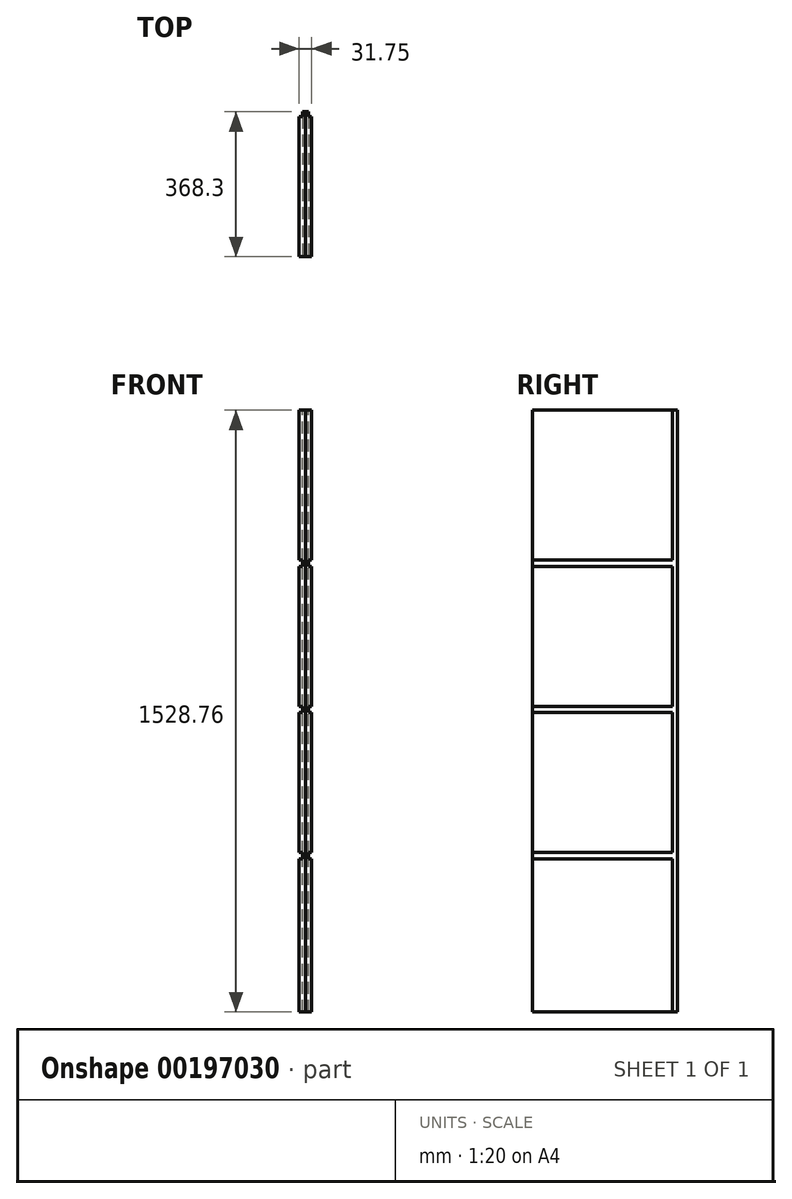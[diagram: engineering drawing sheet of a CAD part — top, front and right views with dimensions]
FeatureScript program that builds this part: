
annotation { "Feature Type Name" : "Feature", "Feature Type Description" : "" }
export const myFeature = defineFeature(function(context is Context, id is Id, definition is map)
    precondition{}
    {
        {
            var Q0;
            Q0=qCreatedBy(makeId("Top.planeOp"),FACE);
            var sketch = newSketch(context, id + "F0", { "sketchPlane" : qUnion([Q0])});
            skLineSegment(sketch, "E0.bottom", {"start": v(0, 0) * mm, "end": v(-15.88, 0) * mm});
            skLineSegment(sketch, "E0.top", {"start": v(0, 368.3) * mm, "end": v(-15.88, 368.3) * mm});
            skLineSegment(sketch, "E0.left", {"start": v(0, 0) * mm, "end": v(0, 368.3) * mm});
            skLineSegment(sketch, "E0.right", {"start": v(-15.88, 0) * mm, "end": v(-15.88, 368.3) * mm});
            skSolve(sketch);
        }
        {
            var Q0;
            Q0=makeQuery(id+"F0.imprint","IMPRINT",FACE,{"disambiguationData":[TD([[makeQuery(id+"F0.imprint","IMPRINT",EDGE,{"derivedFrom":sQuery(id+"F0.wireOp",EDGE,"E0.bottom")}),-1.0]])]});
            extrude(context, id + "F1", {"entities" : qUnion([Q0]), "depth" : 1528.76 * mm});
        }
        {
            var Q0;
            Q0=makeQuery(id+"F1.opExtrude","SWEPT_FACE",FACE,{"disambiguationData":[OSD([sQuery(id+"F0.wireOp",EDGE,"E0.bottom")])]});
            var sketch = newSketch(context, id + "F2", { "sketchPlane" : qUnion([Q0])});
            skLineSegment(sketch, "E1.bottom", {"start": v(0, 404.81) * mm, "end": v(-7.94, 404.81) * mm});
            skLineSegment(sketch, "E1.top", {"start": v(0, 388.94) * mm, "end": v(-7.94, 388.94) * mm});
            skLineSegment(sketch, "E1.left", {"start": v(0, 404.81) * mm, "end": v(0, 388.94) * mm});
            skLineSegment(sketch, "E1.right", {"start": v(-7.94, 404.81) * mm, "end": v(-7.94, 388.94) * mm});
            skLineSegment(sketch, "E2.bottom", {"start": v(0, 776.29) * mm, "end": v(-7.94, 776.29) * mm});
            skLineSegment(sketch, "E2.top", {"start": v(0, 760.41) * mm, "end": v(-7.94, 760.41) * mm});
            skLineSegment(sketch, "E2.left", {"start": v(0, 776.29) * mm, "end": v(0, 760.41) * mm});
            skLineSegment(sketch, "E2.right", {"start": v(-7.94, 776.29) * mm, "end": v(-7.94, 760.41) * mm});
            skLineSegment(sketch, "E3.bottom", {"start": v(0, 1147.76) * mm, "end": v(-7.94, 1147.76) * mm});
            skLineSegment(sketch, "E3.top", {"start": v(0, 1131.89) * mm, "end": v(-7.94, 1131.89) * mm});
            skLineSegment(sketch, "E3.left", {"start": v(0, 1147.76) * mm, "end": v(0, 1131.89) * mm});
            skLineSegment(sketch, "E3.right", {"start": v(-7.94, 1147.76) * mm, "end": v(-7.94, 1131.89) * mm});
            skLineSegment(sketch, "E4.bottom", {"start": v(0, 1516.06) * mm, "end": v(-7.94, 1516.06) * mm});
            skLineSegment(sketch, "E4.top", {"start": v(0, 1531.94) * mm, "end": v(-7.94, 1531.94) * mm});
            skLineSegment(sketch, "E4.left", {"start": v(0, 1516.06) * mm, "end": v(0, 1531.94) * mm});
            skLineSegment(sketch, "E4.right", {"start": v(-7.94, 1516.06) * mm, "end": v(-7.94, 1531.94) * mm});
            skLineSegment(sketch, "E5", {"start": v(-15.88, 0) * mm, "end": v(-15.88, -7.94) * mm, "construction": true});
            skLineSegment(sketch, "E6", {"start": v(-15.88, -7.94) * mm, "end": v(0, -7.94) * mm, "construction": true});
            skLineSegment(sketch, "E7", {"start": v(0, -7.94) * mm, "end": v(0, 0) * mm, "construction": true});
            skLineSegment(sketch, "E8", {"start": v(0, 0) * mm, "end": v(-15.88, 0) * mm, "construction": true});
            skLineSegment(sketch, "E9.bottom", {"start": v(0, -7.94) * mm, "end": v(1508.13, -7.94) * mm, "construction": true});
            skLineSegment(sketch, "E9.top", {"start": v(0, 7.94) * mm, "end": v(1508.13, 7.94) * mm, "construction": true});
            skLineSegment(sketch, "E9.left", {"start": v(0, -7.94) * mm, "end": v(0, 7.94) * mm, "construction": true});
            skLineSegment(sketch, "E9.right", {"start": v(1508.13, -7.94) * mm, "end": v(1508.13, 7.94) * mm, "construction": true});
            skSolve(sketch);
        }
        {
            var Q0;
            Q0=makeQuery(id+"F2.imprint","IMPRINT",FACE,{"disambiguationData":[TD([[makeQuery(id+"F2.imprint","IMPRINT",EDGE,{"derivedFrom":sQuery(id+"F2.wireOp",EDGE,"E1.bottom")}),1.0]])]});
            var Q1;
            Q1=makeQuery(id+"F2.imprint","IMPRINT",FACE,{"disambiguationData":[TD([[makeQuery(id+"F2.imprint","IMPRINT",EDGE,{"derivedFrom":sQuery(id+"F2.wireOp",EDGE,"E2.bottom")}),1.0]])]});
            var Q2;
            Q2=makeQuery(id+"F2.imprint","IMPRINT",FACE,{"disambiguationData":[TD([[makeQuery(id+"F2.imprint","IMPRINT",EDGE,{"derivedFrom":sQuery(id+"F2.wireOp",EDGE,"E3.bottom")}),1.0]])]});
            extrude(context, id + "F3", {"entities" : qUnion([Q0, Q1, Q2]), "operationType" : NewBodyOperationType.REMOVE, "endBound" : BoundingType.UP_TO_NEXT, "oppositeDirection" : true, "depth" : 25.4 * mm});
        }
        {
            var Q0;
            {var subQ1=sQuery(id+"F0.wireOp",EDGE,"E0.left");Q0=makeQuery(id+"F3.boolean.opBoolean","SPLIT",FACE,{"disambiguationData":[TD([makeQuery(id+"F3.opExtrude","SWEPT_FACE",FACE,{"disambiguationData":[OSD([sQuery(id+"F2.wireOp",EDGE,"E1.top")])]})])],"derivedFrom":makeQuery(id+"F1.opExtrude","SWEPT_FACE",FACE,{"disambiguationData":[OSD([subQ1])]})});}
            var sketch = newSketch(context, id + "F4", { "sketchPlane" : qUnion([Q0])});
            skLineSegment(sketch, "E10.bottom", {"start": v(368.3, 0) * mm, "end": v(355.6, 0) * mm});
            skLineSegment(sketch, "E10.top", {"start": v(368.3, 1528.76) * mm, "end": v(355.6, 1528.76) * mm});
            skLineSegment(sketch, "E10.left", {"start": v(368.3, 0) * mm, "end": v(368.3, 1528.76) * mm});
            skLineSegment(sketch, "E10.right", {"start": v(355.6, 0) * mm, "end": v(355.6, 1528.76) * mm});
            skSolve(sketch);
        }
        {
            var Q0;
            {var subQ0=sQuery(id+"F4.wireOp",EDGE,"E10.top");Q0=makeQuery(id+"F4.imprint","IMPRINT",FACE,{"disambiguationData":[TD([[makeQuery(id+"F4.imprint","IMPRINT",EDGE,{"derivedFrom":subQ0}),1.0]])]});}
            var Q1;
            {var subQ0=sQuery(id+"F4.wireOp",EDGE,"E10.bottom");Q1=makeQuery(id+"F4.imprint","IMPRINT",FACE,{"disambiguationData":[TD([[makeQuery(id+"F4.imprint","IMPRINT",EDGE,{"derivedFrom":subQ0}),1.0]])]});}
            extrude(context, id + "F5", {"entities" : qUnion([Q0, Q1]), "operationType" : NewBodyOperationType.REMOVE, "oppositeDirection" : true, "depth" : 7.94 * mm});
        }
        {
            var Q0;
            Q0=makeQuery(id+"F1.opExtrude","SWEPT_BODY",BODY,{"disambiguationData":[OSD([sQuery(id+"F0.wireOp",EDGE,"E0.bottom"),sQuery(id+"F0.wireOp",EDGE,"E0.top"),sQuery(id+"F0.wireOp",EDGE,"E0.left"),sQuery(id+"F0.wireOp",EDGE,"E0.right")])]});
            var Q1;
            Q1=makeQuery(id+"F1.opExtrude","SWEPT_FACE",FACE,{"disambiguationData":[OSD([sQuery(id+"F0.wireOp",EDGE,"E0.right")])]});
            mirror(context, id + "F6", {"entities" : qUnion([Q0]), "mirrorPlane" : qUnion([Q1])});
        }
    });
